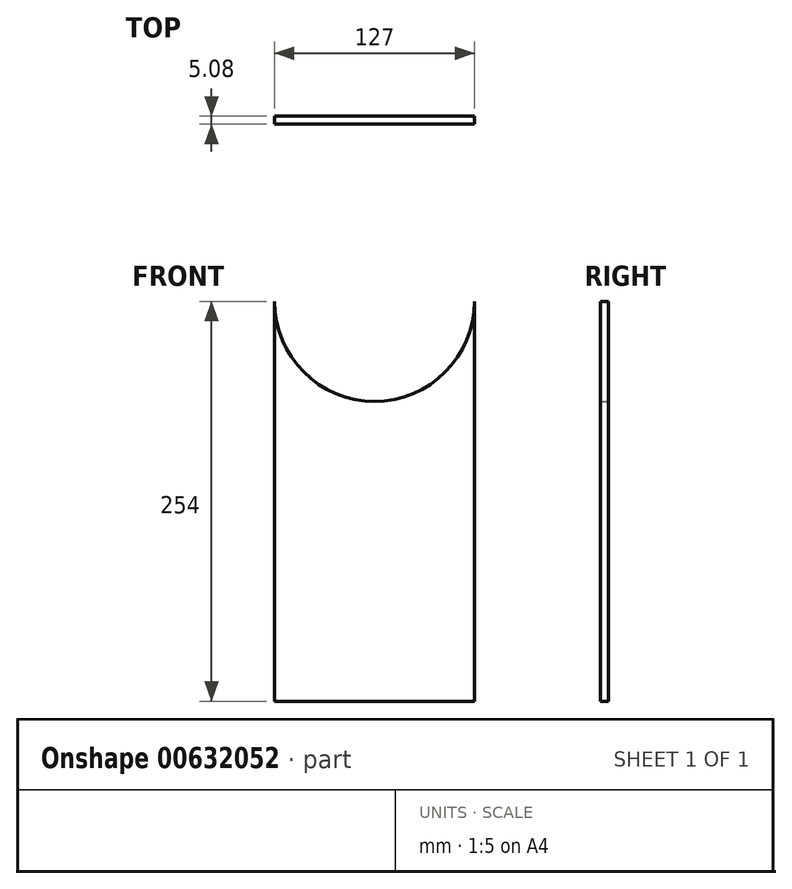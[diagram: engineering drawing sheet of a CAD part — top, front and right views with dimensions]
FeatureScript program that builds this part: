
annotation { "Feature Type Name" : "Feature", "Feature Type Description" : "" }
export const myFeature = defineFeature(function(context is Context, id is Id, definition is map)
    precondition{}
    {
        {
            var Q0;
            Q0=qCreatedBy(makeId("Front.planeOp"),FACE);
            var sketch = newSketch(context, id + "F0", { "sketchPlane" : qUnion([Q0])});
            skLineSegment(sketch, "E0.bottom", {"start": v(0, 0) * mm, "end": v(127, 0) * mm});
            skLineSegment(sketch, "E0.left", {"start": v(0, 0) * mm, "end": v(0, 254) * mm});
            skLineSegment(sketch, "E0.right", {"start": v(127, 0) * mm, "end": v(127, 254) * mm});
            skArc(sketch, "E1", {"start": v(0, 254) * mm, "mid": v(63.5, 190.5) * mm, "end": v(127, 254) * mm});
            skSolve(sketch);
        }
        {
            var Q0;
            Q0 = qSketchRegion(id + "F0", true);
            extrude(context, id + "F1", {"entities" : qUnion([Q0]), "depth" : 5.08 * mm, "offsetDistance" : 25.4 * mm});
        }
    });
